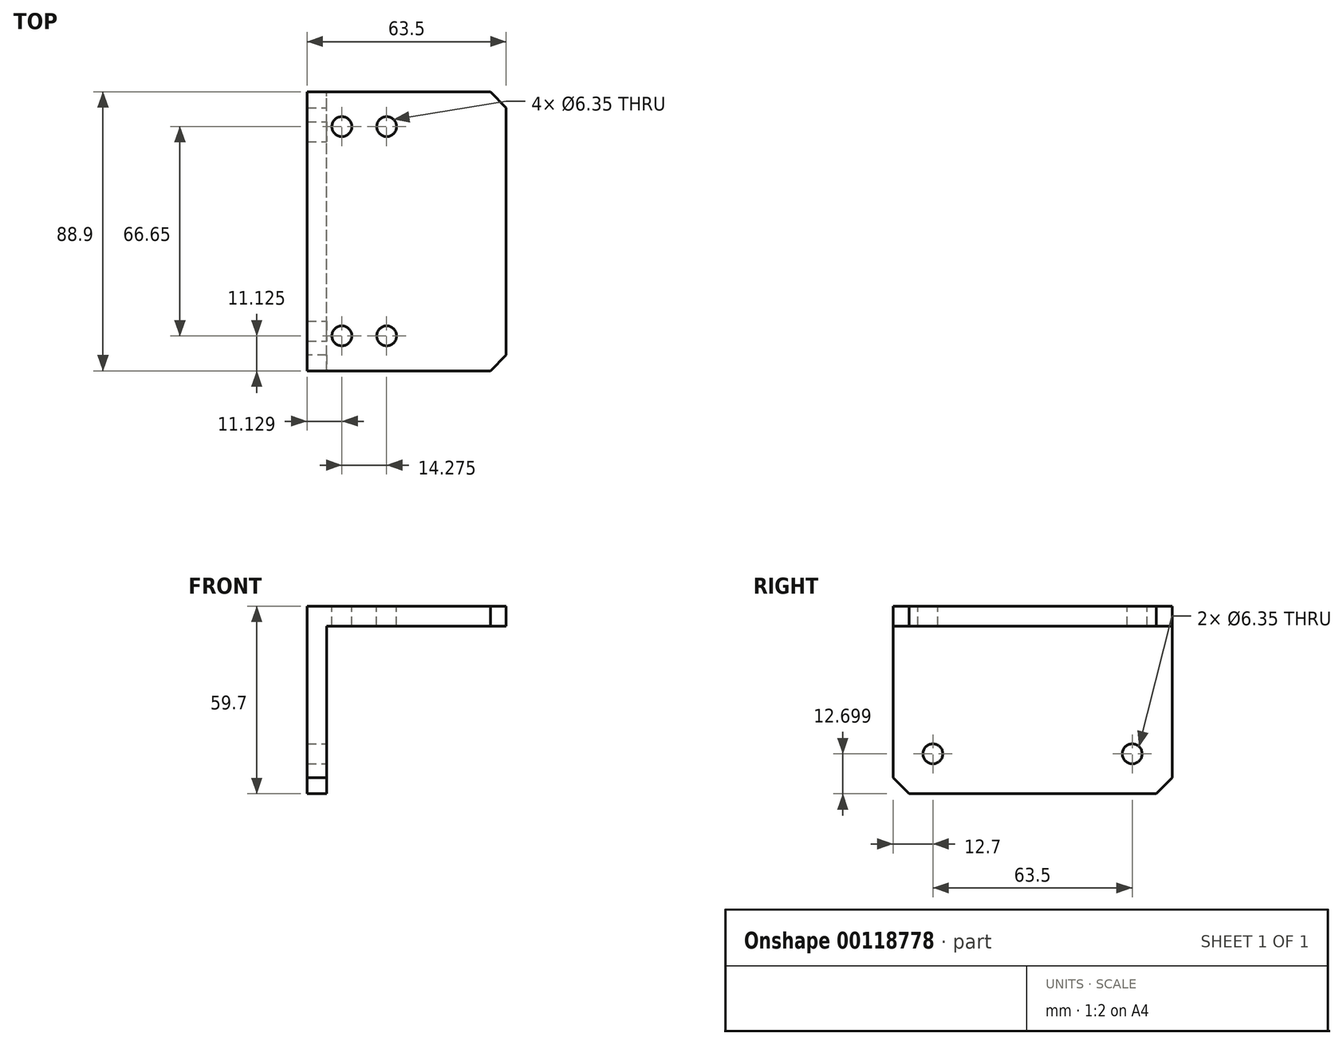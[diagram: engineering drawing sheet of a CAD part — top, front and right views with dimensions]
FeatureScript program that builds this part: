
annotation { "Feature Type Name" : "Feature", "Feature Type Description" : "" }
export const myFeature = defineFeature(function(context is Context, id is Id, definition is map)
    precondition{}
    {
        {
            var Q0;
            Q0=qCreatedBy(makeId("Front.planeOp"),FACE);
            var sketch = newSketch(context, id + "F0", { "sketchPlane" : qUnion([Q0])});
            skLineSegment(sketch, "E0.bottom", {"start": v(-29.43, 33.98) * mm, "end": v(-35.78, 33.98) * mm});
            skLineSegment(sketch, "E0.top", {"start": v(-29.43, -25.72) * mm, "end": v(-35.78, -25.72) * mm});
            skLineSegment(sketch, "E0.left", {"start": v(-29.43, 27.63) * mm, "end": v(-29.43, -25.72) * mm});
            skLineSegment(sketch, "E0.right", {"start": v(-35.78, 33.98) * mm, "end": v(-35.78, -25.72) * mm});
            skLineSegment(sketch, "E1.bottom", {"start": v(-29.43, 33.98) * mm, "end": v(27.72, 33.98) * mm});
            skLineSegment(sketch, "E1.top", {"start": v(-29.43, 27.63) * mm, "end": v(27.72, 27.63) * mm});
            skLineSegment(sketch, "E1.right", {"start": v(27.72, 33.98) * mm, "end": v(27.72, 27.63) * mm});
            skSolve(sketch);
        }
        {
            var Q0;
            Q0 = qSketchRegion(id + "F0", true);
            extrude(context, id + "F1", {"entities" : qUnion([Q0]), "depth" : 88.9 * mm});
        }
        {
            var Q0;
            Q0=makeQuery(id+"F1.opExtrude","SWEPT_FACE",FACE,{"disambiguationData":[OSD([sQuery(id+"F0.wireOp",EDGE,"E0.left")])]});
            var sketch = newSketch(context, id + "F2", { "sketchPlane" : qUnion([Q0])});
            skPoint(sketch, "E2", {"position": v(-76.2, -13.02) * mm});
            skPoint(sketch, "E3", {"position": v(-12.7, -13.02) * mm});
            skSolve(sketch);
        }
        {
            var Q0;
            Q0=sQuery(id+"F2.wireOp",VERTEX,"E2");
            var Q1;
            Q1=sQuery(id+"F2.wireOp",VERTEX,"E3");
            var Q2;
            Q2=makeQuery(id+"F1.opExtrude","SWEPT_BODY",BODY,{"disambiguationData":[OSD([sQuery(id+"F0.wireOp",EDGE,"E0.bottom"),sQuery(id+"F0.wireOp",EDGE,"E0.top"),sQuery(id+"F0.wireOp",EDGE,"E0.left"),sQuery(id+"F0.wireOp",EDGE,"E0.right"),sQuery(id+"F0.wireOp",EDGE,"E1.bottom"),sQuery(id+"F0.wireOp",EDGE,"E1.top"),sQuery(id+"F0.wireOp",EDGE,"E1.right")])]});
            hole(context, id + "F3", {"style" : HoleStyle.SIMPLE, "endStyle" : HoleEndStyle.THROUGH, "holeDiameter" : 6.35 * mm, "locations" : qUnion([Q0, Q1]), "scope" : qUnion([Q2]), "isTappedThrough" : true});
        }
        {
            var Q0;
            Q0=makeQuery(id+"F1.opExtrude","CAP_EDGE",EDGE,{"disambiguationData":[OSD([sQuery(id+"F0.wireOp",EDGE,"E0.top")])],"isStart":false});
            var Q1;
            Q1=makeQuery(id+"F1.opExtrude","CAP_EDGE",EDGE,{"disambiguationData":[OSD([sQuery(id+"F0.wireOp",EDGE,"E1.right")])],"isStart":false});
            var Q2;
            Q2=makeQuery(id+"F1.opExtrude","CAP_EDGE",EDGE,{"disambiguationData":[OSD([sQuery(id+"F0.wireOp",EDGE,"E1.right")])],"isStart":true});
            var Q3;
            Q3=makeQuery(id+"F1.opExtrude","CAP_EDGE",EDGE,{"disambiguationData":[OSD([sQuery(id+"F0.wireOp",EDGE,"E0.top")])],"isStart":true});
            chamfer(context, id + "F4", {"entities" : qUnion([Q0, Q1, Q2, Q3]), "width" : 5.08 * mm, "tangentPropagation" : true});
        }
        {
            var Q0;
            Q0=makeQuery(id+"F1.opExtrude","SWEPT_FACE",FACE,{"disambiguationData":[OSD([sQuery(id+"F0.wireOp",EDGE,"E0.bottom"),sQuery(id+"F0.wireOp",EDGE,"E1.bottom")])]});
            var sketch = newSketch(context, id + "F5", { "sketchPlane" : qUnion([Q0])});
            skPoint(sketch, "E4", {"position": v(-24.65, -11.13) * mm});
            skPoint(sketch, "E5", {"position": v(-10.38, -11.13) * mm});
            skPoint(sketch, "E6", {"position": v(-10.38, -77.77) * mm});
            skPoint(sketch, "E7", {"position": v(-24.65, -77.77) * mm});
            skSolve(sketch);
        }
        {
            var Q0;
            Q0=sQuery(id+"F5.wireOp",VERTEX,"E5");
            var Q1;
            Q1=sQuery(id+"F5.wireOp",VERTEX,"E4");
            var Q2;
            Q2=sQuery(id+"F5.wireOp",VERTEX,"E7");
            var Q3;
            Q3=sQuery(id+"F5.wireOp",VERTEX,"E6");
            var Q4;
            Q4=makeQuery(id+"F1.opExtrude","SWEPT_BODY",BODY,{"disambiguationData":[OSD([sQuery(id+"F0.wireOp",EDGE,"E0.bottom"),sQuery(id+"F0.wireOp",EDGE,"E0.top"),sQuery(id+"F0.wireOp",EDGE,"E0.left"),sQuery(id+"F0.wireOp",EDGE,"E0.right"),sQuery(id+"F0.wireOp",EDGE,"E1.bottom"),sQuery(id+"F0.wireOp",EDGE,"E1.top"),sQuery(id+"F0.wireOp",EDGE,"E1.right")])]});
            hole(context, id + "F6", {"style" : HoleStyle.SIMPLE, "endStyle" : HoleEndStyle.THROUGH, "holeDiameter" : 6.35 * mm, "locations" : qUnion([Q0, Q1, Q2, Q3]), "scope" : qUnion([Q4]), "isTappedThrough" : true});
        }
    });
